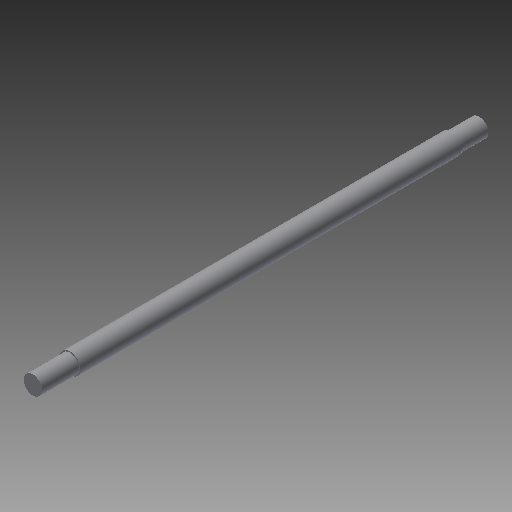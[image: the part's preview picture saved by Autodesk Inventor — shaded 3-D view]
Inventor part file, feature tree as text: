
AUTODESK INVENTOR PART (.ipt)
format: ipt  version: 2018 (Build 220112000, 112)  size: 88,576 bytes
history: native  units: mm
features: revolve x1, sketch x1
ambient origin geometry x8: Origin, YZ Plane, XZ Plane, XY Plane, X Axis, Y Axis, Z Axis, Center Point
bodies: Volumenkörper1 (feature_tree)
feature tree (2):
  revolve  "Umdrehung1"
  sketch  "Skizze1"  dims[d0=2.0mm d1=2.25mm d2=8.0mm d3=88.0mm d4=90.0deg d5=2.0mm d6=6.0mm]
